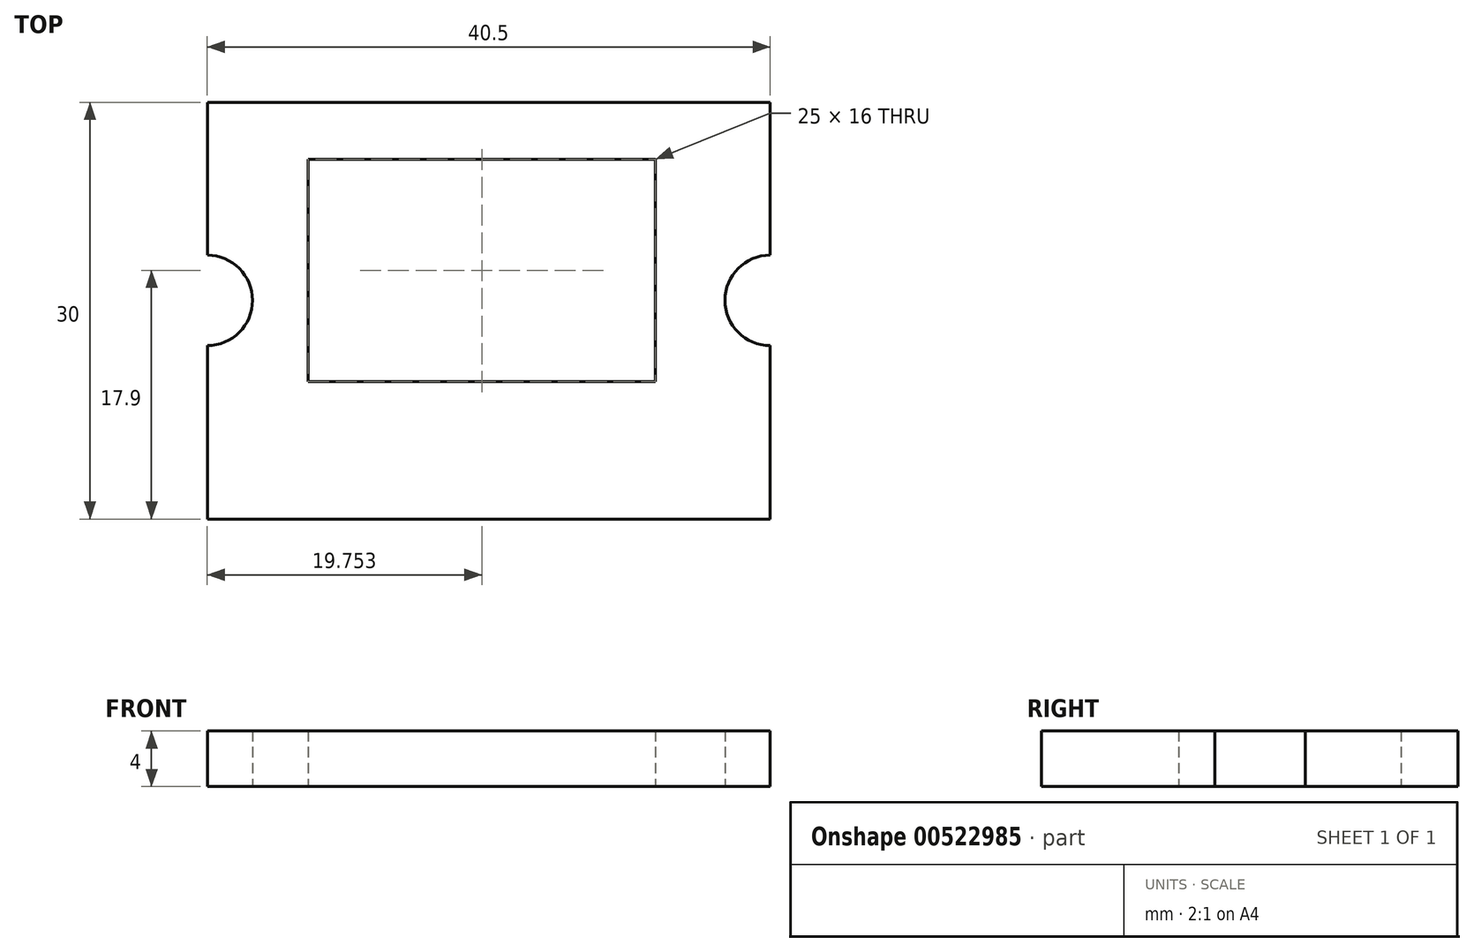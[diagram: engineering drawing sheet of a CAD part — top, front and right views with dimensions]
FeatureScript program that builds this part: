
annotation { "Feature Type Name" : "Feature", "Feature Type Description" : "" }
export const myFeature = defineFeature(function(context is Context, id is Id, definition is map)
    precondition{}
    {
        {
            var Q0;
            Q0=qCreatedBy(makeId("Top.planeOp"),FACE);
            var sketch = newSketch(context, id + "F0", { "sketchPlane" : qUnion([Q0])});
            skLineSegment(sketch, "E0.bottom", {"start": v(-21.15, 20.1) * mm, "end": v(19.35, 20.1) * mm});
            skLineSegment(sketch, "E0.top", {"start": v(-21.15, -9.9) * mm, "end": v(19.35, -9.9) * mm});
            skLineSegment(sketch, "E1.bottom", {"start": v(-13.9, 0) * mm, "end": v(11.1, 0) * mm});
            skLineSegment(sketch, "E1.top", {"start": v(-13.9, 16) * mm, "end": v(11.1, 16) * mm});
            skLineSegment(sketch, "E1.left", {"start": v(-13.9, 0) * mm, "end": v(-13.9, 16) * mm});
            skLineSegment(sketch, "E1.right", {"start": v(11.1, 0) * mm, "end": v(11.1, 16) * mm});
            skArc(sketch, "E2", {"start": v(-21.15, 2.6) * mm, "mid": v(-17.9, 5.85) * mm, "end": v(-21.15, 9.1) * mm});
            skArc(sketch, "E3", {"start": v(19.35, 9.1) * mm, "mid": v(16.1, 5.85) * mm, "end": v(19.35, 2.6) * mm});
            skLineSegment(sketch, "E4", {"start": v(-21.15, 9.1) * mm, "end": v(-21.15, 20.1) * mm});
            skLineSegment(sketch, "E5", {"start": v(-21.15, -9.9) * mm, "end": v(-21.15, 2.6) * mm});
            skLineSegment(sketch, "E6", {"start": v(19.35, 9.1) * mm, "end": v(19.35, 20.1) * mm});
            skLineSegment(sketch, "E7", {"start": v(19.35, 20.1) * mm, "end": v(19.35, 9.1) * mm});
            skLineSegment(sketch, "E8", {"start": v(19.35, 2.6) * mm, "end": v(19.35, -9.9) * mm});
            skSolve(sketch);
        }
        {
            var Q0;
            Q0 = qSketchRegion(id + "F0", true);
            extrude(context, id + "F1", {"entities" : qUnion([Q0]), "depth" : 4 * mm, "offsetDistance" : 25 * mm});
        }
    });
